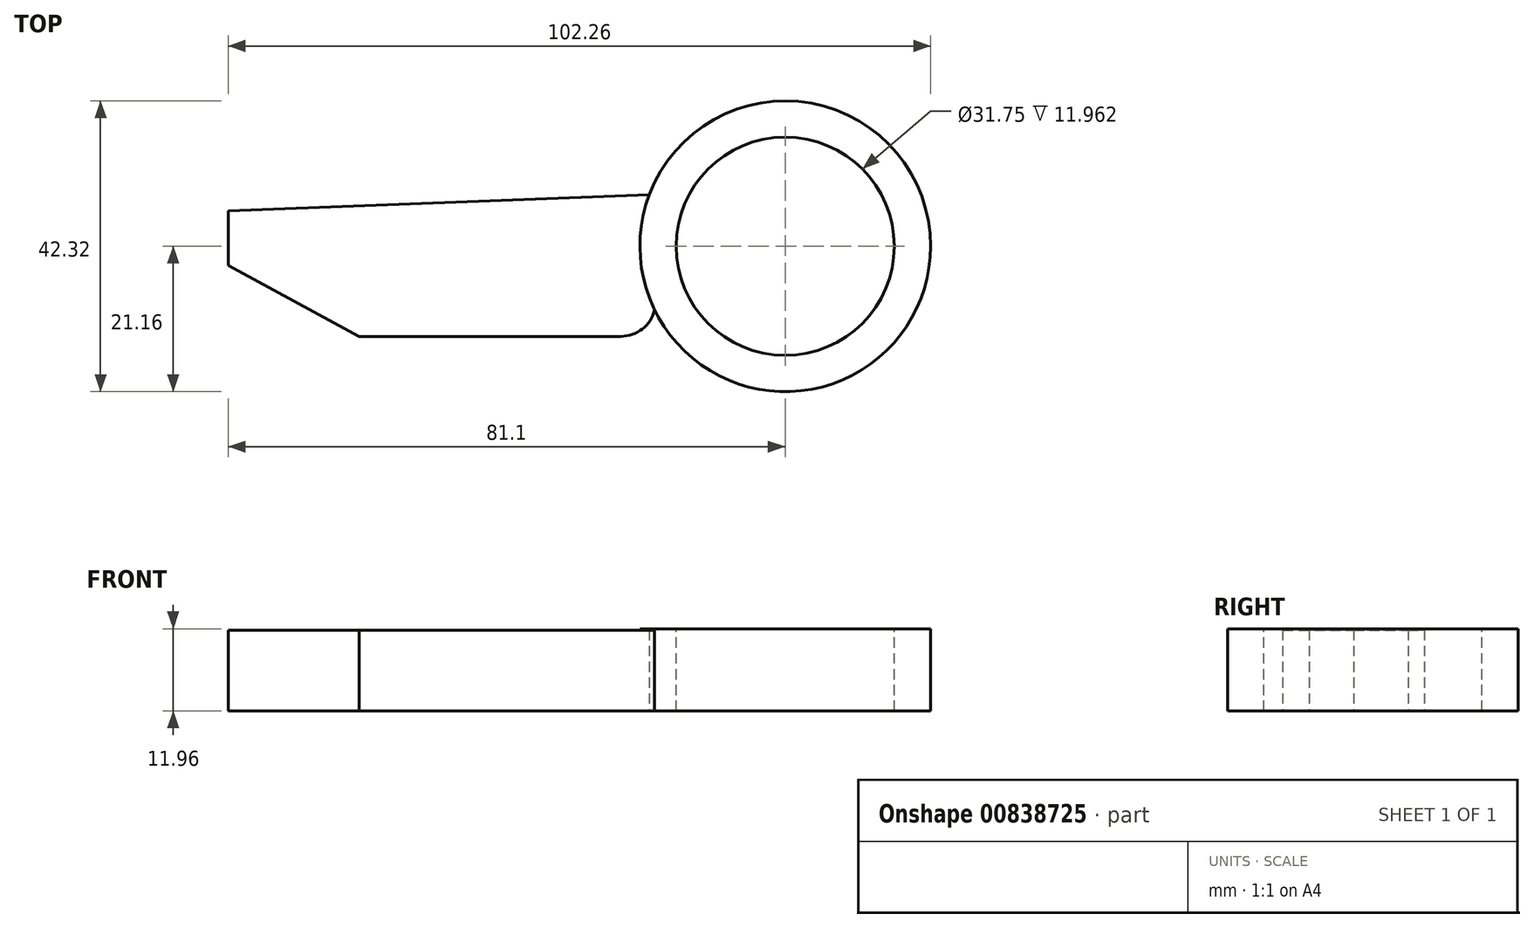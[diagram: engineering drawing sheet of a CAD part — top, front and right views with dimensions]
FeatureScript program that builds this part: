
annotation { "Feature Type Name" : "Feature", "Feature Type Description" : "" }
export const myFeature = defineFeature(function(context is Context, id is Id, definition is map)
    precondition{}
    {
        {
            var Q0;
            Q0=qCreatedBy(makeId("Top.planeOp"),FACE);
            var sketch = newSketch(context, id + "F0", { "sketchPlane" : qUnion([Q0])});
            skCircle(sketch, "E0", {"center": v(0, 0) * mm, "radius": 21.16 * mm});
            skSolve(sketch);
        }
        {
            var Q0;
            Q0=makeQuery(id+"F0.imprint","IMPRINT",FACE,{"disambiguationData":[TD([[makeQuery(id+"F0.imprint","IMPRINT",EDGE,{"derivedFrom":sQuery(id+"F0.wireOp",EDGE,"E0")}),1.0]])]});
            extrude(context, id + "F1", {"entities" : qUnion([Q0]), "depth" : 11.96 * mm, "offsetDistance" : 25.4 * mm});
        }
        {
            var Q0;
            Q0=qCreatedBy(makeId("Top.planeOp"),FACE);
            var sketch = newSketch(context, id + "F2", { "sketchPlane" : qUnion([Q0])});
            skLineSegment(sketch, "E1", {"start": v(-19.01, 7.54) * mm, "end": v(-19.01, -13.11) * mm});
            skLineSegment(sketch, "E2", {"start": v(-19.01, -13.11) * mm, "end": v(-62.02, -13.11) * mm});
            skLineSegment(sketch, "E3", {"start": v(-62.02, -13.11) * mm, "end": v(-81.1, -2.8) * mm});
            skLineSegment(sketch, "E4", {"start": v(-81.1, -2.8) * mm, "end": v(-81.1, 5.13) * mm});
            skLineSegment(sketch, "E5", {"start": v(-81.1, 5.13) * mm, "end": v(-19.01, 7.54) * mm});
            skLineSegment(sketch, "E6", {"start": v(-36.18, 6.87) * mm, "end": v(-59.22, 5.98) * mm});
            skSolve(sketch);
        }
        {
            var Q0;
            {var subQ1=sQuery(id+"F2.wireOp",EDGE,"E1");Q0=makeQuery(id+"F2.imprint","IMPRINT",FACE,{"disambiguationData":[TD([[makeQuery(id+"F2.imprint","IMPRINT",EDGE,{"derivedFrom":subQ1}),-1.0]])]});}
            extrude(context, id + "F3", {"entities" : qUnion([Q0]), "operationType" : NewBodyOperationType.ADD, "depth" : 11.68 * mm, "offsetDistance" : 25.4 * mm});
        }
        {
            var Q0;
            Q0=makeQuery(id+"F3.opExtrude","SWEPT_EDGE",EDGE,{"disambiguationData":[OSD([sQuery(id+"F2.wireOp",EDGE,"E1"),sQuery(id+"F2.wireOp",EDGE,"E2")])]});
            fillet(context, id + "F4", {"entities" : qUnion([Q0]), "radius" : 5.08 * mm, "tangentPropagation" : true, "allowEdgeOverflow" : false});
        }
        {
            var Q0;
            Q0=makeQuery(id+"F3.opExtrude","CAP_FACE",FACE,{"disambiguationData":[OSD([sQuery(id+"F2.wireOp",EDGE,"E1"),sQuery(id+"F2.wireOp",EDGE,"E2"),sQuery(id+"F2.wireOp",EDGE,"E3"),sQuery(id+"F2.wireOp",EDGE,"E4"),sQuery(id+"F2.wireOp",EDGE,"E5"),sQuery(id+"F2.wireOp",EDGE,"E6")])],"isStart":false});
            var sketch = newSketch(context, id + "F5", { "sketchPlane" : qUnion([Q0])});
            skLineSegment(sketch, "E7", {"start": v(-23.93, -13.11) * mm, "end": v(-13.37, -16.22) * mm});
            skSolve(sketch);
        }
        {
            var Q0;
            {var subQ3=sQuery(id+"F2.wireOp",EDGE,"E3");Q0=makeQuery(id+"F5.imprint","IMPRINT",FACE,{"disambiguationData":[TD([[makeQuery(id+"F5.imprint","IMPRINT",EDGE,{"derivedFrom":makeQuery(id+"F3.opExtrude","CAP_EDGE",EDGE,{"disambiguationData":[OSD([subQ3])],"isStart":false})}),-1.0]])]});}
            var Q1;
            Q1=sQuery(id+"F5.wireOp",EDGE,"E7");
            extrude(context, id + "F6", {"entities" : qUnion([Q0]), "operationType" : NewBodyOperationType.ADD, "surfaceEntities" : qUnion([Q1]), "depth" : 0.08 * mm, "offsetDistance" : 25.4 * mm});
        }
        {
            var Q0;
            Q0=makeQuery(id+"F6.opExtrude","CAP_FACE",FACE,{"disambiguationData":[OSD([sQuery(id+"F0.wireOp",EDGE,"E0"),sQuery(id+"F2.wireOp",EDGE,"E1"),sQuery(id+"F2.wireOp",EDGE,"E2"),sQuery(id+"F2.wireOp",EDGE,"E3"),sQuery(id+"F2.wireOp",EDGE,"E4"),sQuery(id+"F2.wireOp",EDGE,"E5"),sQuery(id+"F2.wireOp",EDGE,"E6")])],"isStart":false});
            var sketch = newSketch(context, id + "F7", { "sketchPlane" : qUnion([Q0])});
            skFitSpline(sketch, "E8", {"points": [v(-23.93, -13.11) * mm, v(-10.8, -17.81) * mm, v(-1.95, -23.29) * mm], "startDerivative": vector(25.92, -7.95) * mm, "endDerivative": vector(17.86, -12.51) * mm});
            skSolve(sketch);
        }
        {
            var Q0;
            Q0 = qSketchRegion(id + "F7", true);
            var Q1;
            Q1=sQuery(id+"F7.wireOp",EDGE,"E8");
            extrude(context, id + "F8", {"entities" : qUnion([Q0]), "bodyType" : ToolBodyType.SURFACE, "surfaceEntities" : qUnion([Q1]), "oppositeDirection" : true, "depth" : 11.82 * mm, "offsetDistance" : 25.4 * mm});
        }
        {
            var Q0;
            Q0=makeQuery(id+"F1.opExtrude","CAP_FACE",FACE,{"disambiguationData":[OSD([sQuery(id+"F0.wireOp",EDGE,"E0")])],"isStart":false});
            var sketch = newSketch(context, id + "F9", { "sketchPlane" : qUnion([Q0])});
            skPoint(sketch, "E9", {"position": v(0, 0) * mm});
            skSolve(sketch);
        }
        {
            var Q0;
            Q0=sQuery(id+"F9.wireOp",VERTEX,"E9");
            var Q1;
            Q1=makeQuery(id+"F1.opExtrude","SWEPT_BODY",BODY,{"disambiguationData":[OSD([sQuery(id+"F0.wireOp",EDGE,"E0")])]});
            hole(context, id + "F10", {"style" : HoleStyle.SIMPLE, "endStyle" : HoleEndStyle.THROUGH, "holeDiameter" : 31.75 * mm, "majorDiameter" : 6.35 * mm, "isTappedThrough" : true, "tappedDepth" : 12.7 * mm, "tapClearance" : 3, "locations" : qUnion([Q0]), "scope" : qUnion([Q1])});
        }
    });
